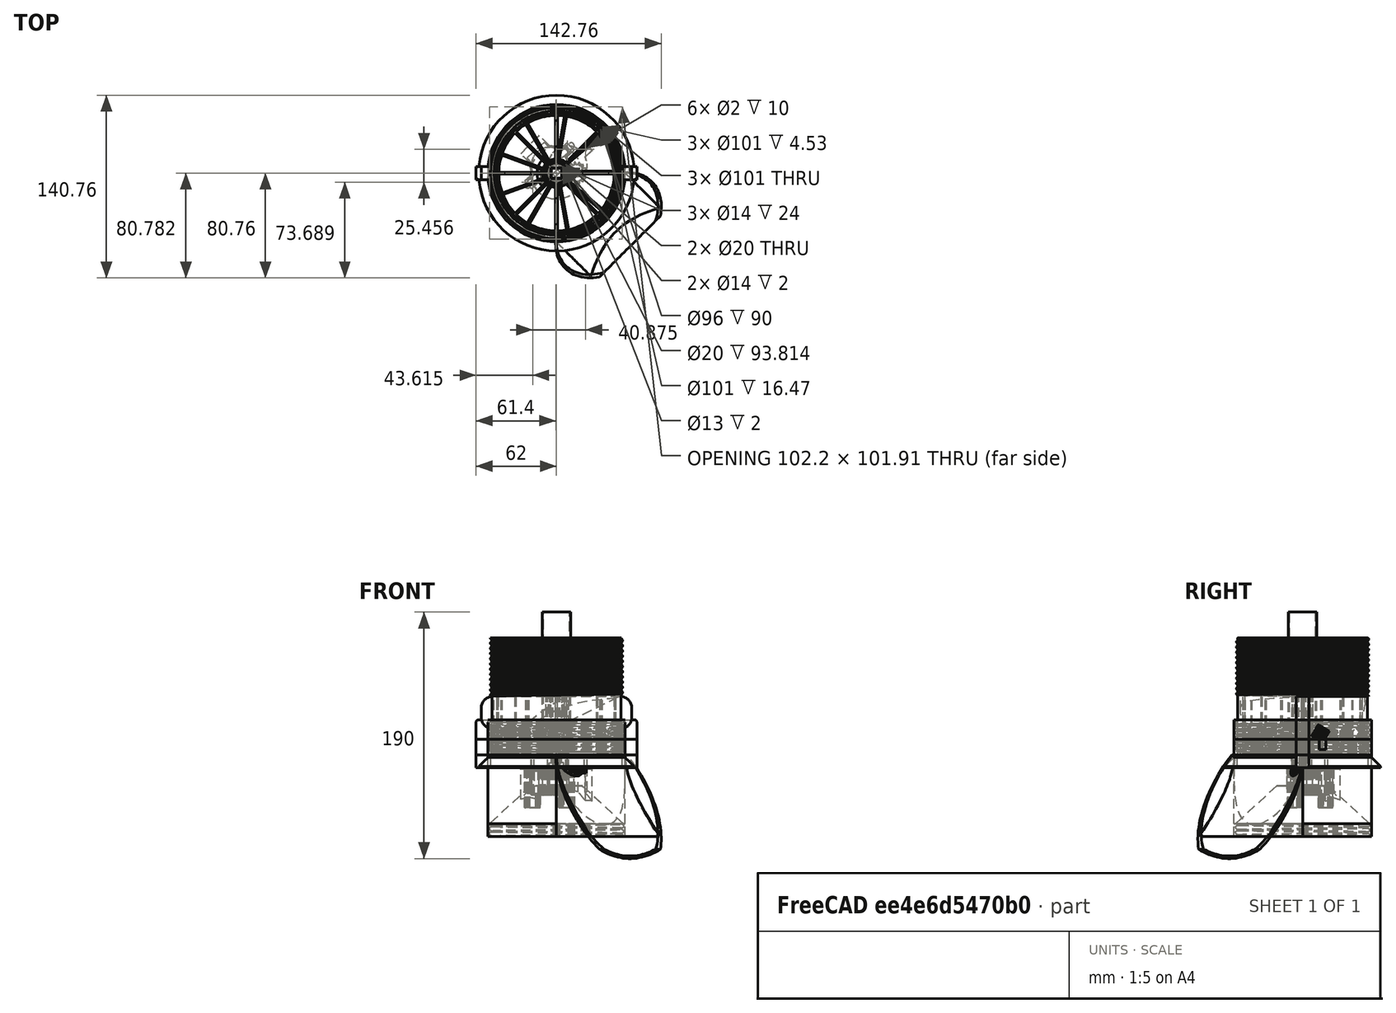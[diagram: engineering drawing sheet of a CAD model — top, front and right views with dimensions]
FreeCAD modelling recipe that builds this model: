
FCSTD DOCUMENT  (FreeCAD 0.19R24291 (Git))
Label: Small
License: CreativeCommons Attribution-NonCommercial
LicenseURL: http://creativecommons.org/licenses/by-nc/4.0/
objects: Part::Box×39, Part::Cylinder×30, Part::MultiFuse×25, Part::Cut×24, Part::FeaturePython×21, Part::Cone×11, App::DocumentObjectGroup×9, Part::Helix×5, PartDesign::FeatureBase×5, Sketcher::SketchObject×5, Part::Sweep×5, Part::Feature×5, Part::Fillet×3, PartDesign::Body×2, Part::Chamfer×1
note: 181 computed .brp shape members not serialized (recipe doc carries the construction recipe); baked Part::Feature solids carry a one-line shape summary decoded from their .brp

FEATURE [Part::Cylinder] Cylinder
  Angle = 270
  AttacherType = Attacher::AttachEngine3D
  Height = 2
  Radius = 53
FEATURE [Part::Box] Box  label="Cube"
  AttacherType = Attacher::AttachEngine3D
  Height = 60
  Length = 100
  Placement = pos=(-47,-0.8,0) rot=(0,0,1;0rad)
  Width = 1.5
FEATURE [Part::FeaturePython] Tube  # WARN: FeaturePython — macro-defined, semantics opaque (R4)
  Height = 60
  InnerRadius = 44.5
  OuterRadius = 46
FEATURE [Part::Box] Box003  label="Cube003"
  AttacherType = Attacher::AttachEngine3D
  Height = 60
  Length = 100
  Placement = pos=(-0.8,48.5,0) rot=(0,0,-1;1.5708rad)
  Width = 1.5
FEATURE [Part::Cylinder] Cylinder001
  Angle = 360
  AttacherType = Attacher::AttachEngine3D
  Height = 60
  Radius = 8
FEATURE [Part::Box] Box004  label="Cube004"
  AttacherType = Attacher::AttachEngine3D
  Height = 60
  Length = 8.3
  Placement = pos=(-4.15,-4.15,0) rot=(0,0,1;0rad)
  Width = 8.3
FEATURE [Part::Cone] Cone
  Angle = 360
  AttacherType = Attacher::AttachEngine3D
  Height = 10
  Placement = pos=(0,0,2) rot=(0,0,1;0rad)
  Radius1 = 7
  Radius2 = 4
FEATURE [Part::FeaturePython] Tube001  label="Tube001_out"  # WARN: FeaturePython — macro-defined, semantics opaque (R4)
  Height = 132
  InnerRadius = 48
  OuterRadius = 50
FEATURE [Part::FeaturePython] Tube002  # WARN: FeaturePython — macro-defined, semantics opaque (R4)
  Height = 2
  InnerRadius = 46
  OuterRadius = 53
FEATURE [Part::FeaturePython] Tube003  # WARN: FeaturePython — macro-defined, semantics opaque (R4)
  Height = 2
  InnerRadius = 4
  OuterRadius = 8.5
FEATURE [Part::Cylinder] Cylinder002
  Angle = 360
  AttacherType = Attacher::AttachEngine3D
  Height = 2
  Radius = 6.5
FEATURE [Part::Cone] Cone001
  Angle = 360
  AttacherType = Attacher::AttachEngine3D
  Height = 30
  Radius1 = 9
  Radius2 = 4
FEATURE [Part::Helix] Helix  label="Helix_in"
  Angle = 0
  AttacherType = Attacher::AttachEngine3D
  Height = 63
  LocalCoord = 0
  Pitch = 4
  Radius = 50
  Style = 1
FEATURE [PartDesign::FeatureBase] BaseFeature
  BaseFeature = -> Helix
FEATURE [Sketcher::SketchObject] Sketch
  ExternalGeometry = -> [BaseFeature]
  FullyConstrained = false
  MapMode = 5
  Placement = pos=(0,0,0) rot=(0.57735,0.57735,0.57735;2.0944rad)
  Support = -> [YZ_Plane]
  sketch-geometry (1):
    g0: Circle CenterX=-50 CenterY=63 CenterZ=0 NormalX=0 NormalY=0 NormalZ=1 AngleXU=0 Radius=1
  constraints (2):
    c: Radius(g0) = 1
    c: Coincident(g0,g-3)
FEATURE [PartDesign::Body] Body
  BaseFeature = -> Helix
  Group = -> [BaseFeature,Sketch]
  Origin = -> Origin
  Tip = -> BaseFeature
FEATURE [Part::Sweep] Sweep  label="Sweep_in"
  Frenet = true
  Sections = -> [Sketch]
  Solid = true
  Spine = -> BaseFeature [Edge16,Edge15,Edge14,Edge13,Edge12,Edge11,Edge10,Edge9,Edge8,Edge7,Edge6,Edge5,Edge4,Edge3,Edge2,Edge1]
  Transition = 1
FEATURE [Part::FeaturePython] Tube004  # WARN: FeaturePython — macro-defined, semantics opaque (R4)
  Height = 20
  InnerRadius = 50
  OuterRadius = 53
  Placement = pos=(0,0,25) rot=(0,0,1;0rad)
FEATURE [Part::Cylinder] Cylinder004
  Angle = 360
  AttacherType = Attacher::AttachEngine3D
  Height = 63
  Placement = pos=(0,0,90) rot=(0,0,1;0rad)
  Radius = 55
FEATURE [Part::Cylinder] Cylinder005
  Angle = 360
  AttacherType = Attacher::AttachEngine3D
  Height = 5
  Placement = pos=(0,0,-5) rot=(0,0,1;0rad)
  Radius = 55
FEATURE [Part::MultiFuse] Fusion003
  Shapes = -> [Tube004,Cylinder004,Cylinder005]
FEATURE [Part::Helix] Helix001  label="Helix_out"
  Angle = 0
  AttacherType = Attacher::AttachEngine3D
  Height = 63
  LocalCoord = 0
  Pitch = 4
  Radius = 50.2
  Style = 1
FEATURE [Part::FeaturePython] Tube005  label="Tube_out_cover"  # WARN: FeaturePython — macro-defined, semantics opaque (R4)
  Height = 10
  InnerRadius = 50.5
  OuterRadius = 53
FEATURE [PartDesign::FeatureBase] BaseFeature001
  BaseFeature = -> Helix001
FEATURE [Sketcher::SketchObject] Sketch001
  ExternalGeometry = -> [BaseFeature001]
  FullyConstrained = false
  MapMode = 5
  Placement = pos=(0,0,0) rot=(1,0,0;1.5708rad)
  Support = -> [XZ_Plane001]
  sketch-geometry (1):
    g0: Circle CenterX=50.2 CenterY=0 CenterZ=0 NormalX=0 NormalY=0 NormalZ=1 AngleXU=0 Radius=1.5
  constraints (2):
    c: Radius(g0) = 1.5
    c: Coincident(g0,g-3)
FEATURE [PartDesign::Body] Body001
  BaseFeature = -> Helix001
  Group = -> [BaseFeature001,Sketch001]
  Origin = -> Origin001
  Tip = -> BaseFeature001
FEATURE [Part::Sweep] Sweep001  label="Sweep_out"
  Frenet = true
  Sections = -> [Sketch001]
  Solid = true
  Spine = -> BaseFeature001 [Edge1,Edge2,Edge3,Edge4,Edge5,Edge6,Edge7,Edge8,Edge9,Edge10,Edge11,Edge12,Edge13,Edge14,Edge15,Edge16]
  Transition = 1
FEATURE [App::DocumentObjectGroup] Group  label="Cut_okraj"
  Group = -> [Body001,Helix001,Sweep001]
FEATURE [Part::Cut] Cut002  label="Cut_kryt001"
  Base = -> Tube005
  Placement = pos=(0,0,2) rot=(0,0,1;0rad)
  Tool = -> Sweep001
FEATURE [Part::MultiFuse] Fusion004
  Shapes = -> [Cylinder,Tube003,Tube002,Cut002]
FEATURE [Part::Cut] Cut003  label="Cut003_vrch"
  Base = -> Fusion004
  Tool = -> Cylinder002
FEATURE [Part::Cylinder] Cylinder006
  Angle = 360
  AttacherType = Attacher::AttachEngine3D
  Height = 53
  Placement = pos=(0,0,-53) rot=(0,0,1;0rad)
  Radius = 53
FEATURE [Part::Cylinder] Cylinder007
  Angle = 360
  AttacherType = Attacher::AttachEngine3D
  Height = 45
  Placement = pos=(0,0,-43) rot=(0,0,1;0rad)
  Radius = 8.5
FEATURE [Part::FeaturePython] Tube009  # WARN: FeaturePython — macro-defined, semantics opaque (R4)
  Height = 53
  InnerRadius = 7
  OuterRadius = 8.5
  Placement = pos=(0,0,-53) rot=(0,0,1;0rad)
FEATURE [Part::Cone] Cone002  label="Cone002_vonkajsi"
  Angle = 180
  AttacherType = Attacher::AttachEngine3D
  Height = 80
  Placement = pos=(0,0,0) rot=(-0.281085,0.678598,-0.678598;2.59356rad)
  Radius1 = 2
  Radius2 = 80
FEATURE [Part::Cone] Cone003
  Angle = 180
  AttacherType = Attacher::AttachEngine3D
  Height = 80
  Placement = pos=(0,0,0) rot=(-0.281085,0.678598,-0.678598;2.59356rad)
  Radius1 = 2
  Radius2 = 78
FEATURE [Part::Box] Box005  label="Cube005"
  AttacherType = Attacher::AttachEngine3D
  Height = 50
  Length = 100
  Placement = pos=(-38.1838,-91.9239,0) rot=(0.318976,0.770076,-0.552483;1.28666rad)
  Width = 200
FEATURE [Part::FeaturePython] Tube012  label="Tube_out_cover001"  # WARN: FeaturePython — macro-defined, semantics opaque (R4)
  Height = 10
  InnerRadius = 50.5
  OuterRadius = 53
FEATURE [Part::Cylinder] Cylinder008
  Angle = 360
  AttacherType = Attacher::AttachEngine3D
  Height = 2
  Radius = 53
FEATURE [Part::Helix] Helix002  label="Helix_out001"
  Angle = 0
  AttacherType = Attacher::AttachEngine3D
  Height = 63
  LocalCoord = 0
  Pitch = 4
  Radius = 50.2
  Style = 1
FEATURE [PartDesign::FeatureBase] BaseFeature002
  BaseFeature = -> Helix002
FEATURE [Sketcher::SketchObject] Sketch002
  ExternalGeometry = -> [BaseFeature002]
  FullyConstrained = false
  MapMode = 5
  Placement = pos=(0,0,0) rot=(1,0,0;1.5708rad)
  Support = -> [XZ_Plane002]
  sketch-geometry (1):
    g0: Circle CenterX=50.2 CenterY=0 CenterZ=0 NormalX=0 NormalY=0 NormalZ=1 AngleXU=0 Radius=1.5
  constraints (2):
    c: Radius(g0) = 1.5
    c: Coincident(g0,g-3)
FEATURE [Part::Sweep] Sweep002  label="Sweep_out001"
  Frenet = true
  Sections = -> [Sketch002]
  Solid = true
  Spine = -> BaseFeature002 [Edge1,Edge2,Edge3,Edge4,Edge5,Edge6,Edge7,Edge8,Edge9,Edge10,Edge11,Edge12,Edge13,Edge14,Edge15,Edge16]
  Transition = 1
FEATURE [Part::Cut] Cut008  label="Cut_kryt002"
  Base = -> Tube012
  Placement = pos=(0,0,2) rot=(0,0,1;0rad)
  Tool = -> Sweep002
FEATURE [Part::Box] Box006  label="Cube006"
  AttacherType = Attacher::AttachEngine3D
  Height = 12
  Length = 10
  Placement = pos=(52,-5,0) rot=(0,0,1;0rad)
  Width = 10
FEATURE [Part::Box] Box007  label="Cube007"
  AttacherType = Attacher::AttachEngine3D
  Height = 12
  Length = 10
  Placement = pos=(-62,-5,0) rot=(0,0,1;0rad)
  Width = 10
FEATURE [Part::MultiFuse] Fusion007
  Shapes = -> [Cylinder008,Cut008,Box006,Box007]
FEATURE [App::DocumentObjectGroup] Group005  label="horna_krytka"
  Group = -> [BaseFeature002,XZ_Plane002,Helix002,Fusion007]
FEATURE [Part::Box] Box008  label="Cube008"
  AttacherType = Attacher::AttachEngine3D
  Height = 25
  Length = 10
  Placement = pos=(48,-5,20) rot=(0,0,1;0rad)
  Width = 10
FEATURE [Part::Box] Box009  label="Cube009"
  AttacherType = Attacher::AttachEngine3D
  Height = 25
  Length = 10
  Placement = pos=(-58,-5,20) rot=(0,0,1;0rad)
  Width = 10
FEATURE [Part::MultiFuse] Fusion008
  Shapes = -> [Box008,Box009]
FEATURE [Part::Feature] Step_28BYJ_48_V2_positive_CUT001001_solid  label="Step_28BYJ_48_V2_positive_CUT002 (Solid)"
  Placement = pos=(-5.40614,5.8826,-21) rot=(0,0,-1;0.837758rad)
  shape: bbox 38.19 x 35.33 x 39.75 mm, 702 faces (baked)
FEATURE [Part::Cylinder] Cylinder009
  Angle = 360
  AttacherType = Attacher::AttachEngine3D
  Height = 80
  Placement = pos=(-5.42314,5.90251,-91) rot=(0,0,1;0.680678rad)
  Radius = 15
FEATURE [Part::Box] Box010  label="Cube010"
  AttacherType = Attacher::AttachEngine3D
  Height = 80
  Length = 44
  Placement = pos=(-19.1279,-11.9828,-91) rot=(0,0,1;0.733038rad)
  Width = 8
FEATURE [Part::Box] Box011  label="Cube011"
  AttacherType = Attacher::AttachEngine3D
  Height = 80
  Length = 20
  Placement = pos=(-19.799,7.07107,-91) rot=(0,0,1;0.785398rad)
  Width = 11
FEATURE [Part::Box] Box012  label="Cube012"
  AttacherType = Attacher::AttachEngine3D
  Height = 10
  Length = 8
  Placement = pos=(-3.18198,-3.88909,0) rot=(0,0,1;0rad)
  Width = 8
FEATURE [Part::Cone] Cone004
  Angle = 360
  AttacherType = Attacher::AttachEngine3D
  Height = 29
  Placement = pos=(0,0,-53) rot=(0,0,1;0rad)
  Radius1 = 51.5
  Radius2 = 20
FEATURE [Part::Cylinder] Cylinder010
  Angle = 360
  AttacherType = Attacher::AttachEngine3D
  Height = 10
  Placement = pos=(-18.3848,-7.07107,-11) rot=(0,0,1;0.785398rad)
  Radius = 1
FEATURE [Part::Cylinder] Cylinder011
  Angle = 360
  AttacherType = Attacher::AttachEngine3D
  Height = 10
  Placement = pos=(8.48528,18.3848,-11) rot=(0,0,1;0.785398rad)
  Radius = 1
FEATURE [Part::MultiFuse] Fusion010
  Shapes = -> [Box011,Cylinder009,Box010,Cone004,Cylinder010,Cylinder011]
FEATURE [Part::Feature] Cut002001  label="Cut_kryt003"
  Placement = pos=(0,0,-63) rot=(0,0,1;0rad)
  shape: bbox 111.8 x 118.9 x 17.7 mm, 14 faces (baked)
FEATURE [Part::Feature] Cut009001  label="Cut009_middle001"
  shape: bbox 166.1 x 166.1 x 80 mm, 45 faces (baked)
FEATURE [Part::Cylinder] Cylinder013
  Angle = 360
  AttacherType = Attacher::AttachEngine3D
  Height = 3
  Placement = pos=(0,0,-9) rot=(0,0,1;0rad)
  Radius = 5.6
FEATURE [Part::Box] Box014  label="Cube014"
  AttacherType = Attacher::AttachEngine3D
  Height = 40
  Length = 7.9
  Placement = pos=(-4,-4,-6) rot=(0,0,1;0rad)
  Width = 7.9
FEATURE [Part::Cylinder] Cylinder014
  Angle = 360
  AttacherType = Attacher::AttachEngine3D
  Height = 2
  Radius = 7
FEATURE [Part::Box] Box016  label="Cube016"
  AttacherType = Attacher::AttachEngine3D
  Height = 100
  Length = 100
  Placement = pos=(-71.3207,-123.154,-92) rot=(0,0,-1;0.785398rad)
  Width = 100
FEATURE [Part::Box] Box017  label="Cube017"
  AttacherType = Attacher::AttachEngine3D
  Height = 100
  Length = 100
  Placement = pos=(53.0309,0.0406241,-92) rot=(0,0,-1;0.785398rad)
  Width = 100
FEATURE [Part::Box] Box018  label="Cube018"
  AttacherType = Attacher::AttachEngine3D
  Height = 200
  Length = 200
  Placement = pos=(-111,-128,-263) rot=(0,0,1;0rad)
  Width = 200
FEATURE [Part::MultiFuse] Fusion009004
  Shapes = -> [Cone003,Box016,Box017,Box018]
FEATURE [Part::Cut] Cut004  label="Cut004_len_lievik"
  Base = -> Cone002
  Tool = -> Fusion009004
FEATURE [Part::Cut] Cut007
  Base = -> Cut004
  Tool = -> Box005
FEATURE [Part::Box] Box019  label="Cube019"
  AttacherType = Attacher::AttachEngine3D
  Height = 63
  Length = 38
  Placement = pos=(-0.609979,-52.4438,-63) rot=(0,0,-1;0.785398rad)
  Width = 75
FEATURE [Part::Cylinder] Cylinder018
  Angle = 360
  AttacherType = Attacher::AttachEngine3D
  Height = 60
  Placement = pos=(0,0,-63) rot=(0,0,1;0rad)
  Radius = 53
FEATURE [Part::Cut] Cut009005
  Base = -> Box019
  Tool = -> Cylinder018
FEATURE [Part::MultiFuse] Fusion009005
  Shapes = -> [Cylinder006,Cut009005]
FEATURE [Part::Cut] Cut005  label="Cut005_okraj_stena"
  Base = -> Fusion009005
  Tool = -> Cone002
FEATURE [Part::MultiFuse] Fusion005
  Shapes = -> [Cut005,Cut007]
FEATURE [Part::Cut] Cut006
  Base = -> Fusion005
  Tool = -> Cylinder007
FEATURE [Part::MultiFuse] Fusion006  label="spodok"
  Shapes = -> [Tube009,Cut006]
FEATURE [Part::Cut] Cut009  label="Cut009_middle"
  Base = -> Fusion006
  Tool = -> Fusion010
FEATURE [App::DocumentObjectGroup] Group004  label="Spodok"
  Group = -> [Cut003,Cut009,Cut002001]
FEATURE [Part::Fillet] Fillet
  Base = -> Fusion008
  Edges = 4 edges r=9: [Edge6,Edge8,Edge14,Edge16]
FEATURE [Part::Box] Box020  label="Cube020"
  AttacherType = Attacher::AttachEngine3D
  Height = 37
  Length = 10
  Placement = pos=(52,-5,-10) rot=(0,0,1;0rad)
  Width = 10
FEATURE [Part::Cylinder] Cylinder019
  Angle = 360
  AttacherType = Attacher::AttachEngine3D
  Height = 1
  Placement = pos=(0,0,-10) rot=(0,0,1;0rad)
  Radius = 53
FEATURE [Part::Box] Box021  label="Cube021"
  AttacherType = Attacher::AttachEngine3D
  Height = 37
  Length = 10
  Placement = pos=(-62,-5,-10) rot=(0,0,1;0rad)
  Width = 10
FEATURE [Part::FeaturePython] Tube013  label="Tube_out_cover002"  # WARN: FeaturePython — macro-defined, semantics opaque (R4)
  Height = 25
  InnerRadius = 50.5
  OuterRadius = 53
FEATURE [Part::Helix] Helix003  label="Helix_out002"
  Angle = 0
  AttacherType = Attacher::AttachEngine3D
  Height = 63
  LocalCoord = 0
  Pitch = 4
  Radius = 50.2
  Style = 1
FEATURE [PartDesign::FeatureBase] BaseFeature003
  BaseFeature = -> Helix003
FEATURE [Sketcher::SketchObject] Sketch003
  ExternalGeometry = -> [BaseFeature003]
  FullyConstrained = false
  MapMode = 5
  Placement = pos=(0,0,0) rot=(1,0,0;1.5708rad)
  Support = -> [XZ_Plane003]
  sketch-geometry (1):
    g0: Circle CenterX=50.2 CenterY=0 CenterZ=0 NormalX=0 NormalY=0 NormalZ=1 AngleXU=0 Radius=1.5
  constraints (2):
    c: Radius(g0) = 1.5
    c: Coincident(g0,g-3)
FEATURE [Part::Sweep] Sweep003  label="Sweep_out002"
  Frenet = true
  Sections = -> [Sketch003]
  Solid = true
  Spine = -> BaseFeature003 [Edge1,Edge2,Edge3,Edge4,Edge5,Edge6,Edge7,Edge8,Edge9,Edge10,Edge11,Edge12,Edge13,Edge14,Edge15,Edge16]
  Transition = 1
FEATURE [Part::Cut] Cut009006  label="Cut_kryt004"
  Base = -> Tube013
  Placement = pos=(0,0,2) rot=(0,0,1;0rad)
  Tool = -> Sweep003
FEATURE [Part::FeaturePython] Tube014  label="Tube_out_cover003"  # WARN: FeaturePython — macro-defined, semantics opaque (R4)
  Height = 20
  InnerRadius = 50.5
  OuterRadius = 53
  Placement = pos=(0,0,-10) rot=(0,0,1;0rad)
FEATURE [Part::Box] Box022  label="Cube022"
  AttacherType = Attacher::AttachEngine3D
  Height = 10
  Length = 10
  Placement = pos=(84.8787,7,14.5355) rot=(-0.250563,0.250563,0.935113;1.63783rad)
  Width = 156
FEATURE [Part::Box] Box023  label="Cube023"
  AttacherType = Attacher::AttachEngine3D
  Height = 10
  Length = 5
  Placement = pos=(61.306,12.7496,4) rot=(0,0,1;1.5708rad)
  Width = 150
FEATURE [Part::MultiFuse] Fusion009007
  Shapes = -> [Box022,Box023]
FEATURE [Part::Box] Box024  label="Cube024"
  AttacherType = Attacher::AttachEngine3D
  Height = 60
  Length = 100
  Placement = pos=(-32.9993,-34.0926,0) rot=(0,0,1;0.785398rad)
  Width = 1.5
FEATURE [Part::Box] Box025  label="Cube025"
  AttacherType = Attacher::AttachEngine3D
  Height = 60
  Length = 100
  Placement = pos=(34.388,-33.4562,0) rot=(0,0,1;2.35619rad)
  Width = 1.5
FEATURE [Part::MultiFuse] Fusion
  Shapes = -> [Box,Box003,Cylinder001,Tube,Cone001,Box024,Box025]
FEATURE [Part::FeaturePython] Tube015  # WARN: FeaturePython — macro-defined, semantics opaque (R4)
  Height = 60
  InnerRadius = 46
  OuterRadius = 60
FEATURE [Part::MultiFuse] Fusion001
  Shapes = -> [Box004,Cone,Cylinder014,Tube015]
FEATURE [Part::Cut] Cut  label="Cut_vnutro"
  Base = -> Fusion
  Placement = pos=(0,0,2.5) rot=(0,0,1;0rad)
  Tool = -> Fusion001
FEATURE [App::DocumentObjectGroup] Group003  label="Rotacia_6"
  Group = -> [Cut]
FEATURE [Part::Box] Box026  label="Cube026"
  AttacherType = Attacher::AttachEngine3D
  Height = 60
  Length = 50
  Width = 1.5
FEATURE [Part::Cone] Cone005
  Angle = 360
  AttacherType = Attacher::AttachEngine3D
  Height = 10
  Placement = pos=(0,0,2) rot=(0,0,1;0rad)
  Radius1 = 7
  Radius2 = 4
FEATURE [Part::Cone] Cone006
  Angle = 360
  AttacherType = Attacher::AttachEngine3D
  Height = 30
  Radius1 = 9
  Radius2 = 4
FEATURE [Part::FeaturePython] Tube016  # WARN: FeaturePython — macro-defined, semantics opaque (R4)
  Height = 60
  InnerRadius = 45
  OuterRadius = 46
FEATURE [Part::Cylinder] Cylinder020
  Angle = 360
  AttacherType = Attacher::AttachEngine3D
  Height = 60
  Radius = 8
FEATURE [Part::Box] Box028  label="Cube028"
  AttacherType = Attacher::AttachEngine3D
  Height = 60
  Length = 8.4
  Placement = pos=(-4.2,-4.2,0) rot=(0,0,1;0rad)
  Width = 8.4
FEATURE [Part::Cylinder] Cylinder021
  Angle = 360
  AttacherType = Attacher::AttachEngine3D
  Height = 2
  Radius = 7
FEATURE [Part::FeaturePython] Tube017  # WARN: FeaturePython — macro-defined, semantics opaque (R4)
  Height = 60
  InnerRadius = 46
  OuterRadius = 60
FEATURE [Part::MultiFuse] Fusion009008
  Shapes = -> [Box028,Cone005,Cylinder021,Tube017]
FEATURE [Part::Box] Box029  label="Cube029"
  AttacherType = Attacher::AttachEngine3D
  Height = 60
  Length = 50
  Placement = pos=(0,0,0) rot=(0,0,1;0.698132rad)
  Width = 1.5
FEATURE [Part::Box] Box030  label="Cube030"
  AttacherType = Attacher::AttachEngine3D
  Height = 60
  Length = 50
  Placement = pos=(0,0,0) rot=(0,0,1;1.39626rad)
  Width = 1.5
FEATURE [Part::Box] Box031  label="Cube031"
  AttacherType = Attacher::AttachEngine3D
  Height = 60
  Length = 50
  Placement = pos=(0,0,0) rot=(0,0,1;2.0944rad)
  Width = 1.5
FEATURE [Part::Box] Box032  label="Cube032"
  AttacherType = Attacher::AttachEngine3D
  Height = 60
  Length = 50
  Placement = pos=(0,0,0) rot=(0,0,1;2.79253rad)
  Width = 1.5
FEATURE [Part::Box] Box033  label="Cube033"
  AttacherType = Attacher::AttachEngine3D
  Height = 60
  Length = 50
  Placement = pos=(0,0,0) rot=(0,0,1;3.49066rad)
  Width = 1.5
FEATURE [Part::Box] Box034  label="Cube034"
  AttacherType = Attacher::AttachEngine3D
  Height = 60
  Length = 50
  Placement = pos=(0,0,0) rot=(0,0,-1;0.698132rad)
  Width = 1.5
FEATURE [Part::Box] Box035  label="Cube035"
  AttacherType = Attacher::AttachEngine3D
  Height = 60
  Length = 50
  Placement = pos=(0,0,0) rot=(0,0,1;4.88692rad)
  Width = 1.5
FEATURE [Part::Box] Box036  label="Cube036"
  AttacherType = Attacher::AttachEngine3D
  Height = 60
  Length = 50
  Placement = pos=(0,0,0) rot=(0,0,1;4.18879rad)
  Width = 1.5
FEATURE [Part::Box] Box037  label="Cube037"
  AttacherType = Attacher::AttachEngine3D
  Height = 60
  Length = 50
  Placement = pos=(0,0,0) rot=(0,0,1;3.49066rad)
  Width = 1.5
FEATURE [Part::MultiFuse] Fusion009009
  Shapes = -> [Box026,Cylinder020,Tube016,Cone006,Box029,Box030,Box031,Box032,Box033,Box034,Box035,Box036,Box037]
FEATURE [Part::Cut] Cut009008  label="Cut_vnutro001"
  Base = -> Fusion009009
  Tool = -> Fusion009008
FEATURE [App::DocumentObjectGroup] Group009  label="Rotacia_9"
  Group = -> [Cut009008]
FEATURE [Part::FeaturePython] involutegear  # WARN: FeaturePython — macro-defined, semantics opaque (R4)
  AttacherType = Attacher::AttachEngine3D
  Placement = pos=(0,0,-14) rot=(0,0,1;0rad)
  backlash = 0
  beta = 0
  clearance = 0.25
  da = 17
  df = 12.5
  double_helix = false
  dw = 15
  head = 0
  height = 5
  module = 1
  numpoints = 6
  pressure_angle = 20
  properties_from_tool = false
  reversed_backlash = false
  shift = 0
  simple = false
  teeth = 15
  transverse_pitch = 3.14159
  undercut = false
  version = 0.0.3
FEATURE [Part::MultiFuse] Fusion011
  Shapes = -> [Box014,Cylinder013,involutegear]
FEATURE [App::DocumentObjectGroup] Group006  label="Hriadel"
  Group = -> [Fusion011]
FEATURE [Part::Box] Box038  label="Cube038"
  AttacherType = Attacher::AttachEngine3D
  Height = 50
  Length = 100
  Placement = pos=(-38.1838,-91.9239,0) rot=(0.318976,0.770076,-0.552483;1.28666rad)
  Width = 200
FEATURE [Part::Box] Box039  label="Cube039"
  AttacherType = Attacher::AttachEngine3D
  Height = 80
  Length = 44
  Placement = pos=(-5.13,-11.9828,-91) rot=(0,0,1;0.733038rad)
  Width = 8
FEATURE [Part::Cylinder] Cylinder022
  Angle = 360
  AttacherType = Attacher::AttachEngine3D
  Height = 80
  Placement = pos=(8.58,5.90251,-91) rot=(0,0,1;0.680678rad)
  Radius = 15
FEATURE [Part::Cylinder] Cylinder023
  Angle = 360
  AttacherType = Attacher::AttachEngine3D
  Height = 10
  Placement = pos=(-18.38,-7.07107,-11) rot=(0,0,1;0.785398rad)
  Radius = 1
FEATURE [Part::Cylinder] Cylinder024
  Angle = 360
  AttacherType = Attacher::AttachEngine3D
  Height = 10
  Placement = pos=(22.49,18.3848,-11) rot=(0,0,1;0.785398rad)
  Radius = 1
FEATURE [Part::Cylinder] Cylinder025
  Angle = 360
  AttacherType = Attacher::AttachEngine3D
  Height = 53
  Placement = pos=(0,0,-53) rot=(0,0,1;0rad)
  Radius = 53
FEATURE [Part::Cylinder] Cylinder026
  Angle = 360
  AttacherType = Attacher::AttachEngine3D
  Height = 45
  Placement = pos=(0,0,-43) rot=(0,0,1;0rad)
  Radius = 8.5
FEATURE [Part::FeaturePython] Tube018  # WARN: FeaturePython — macro-defined, semantics opaque (R4)
  Height = 53
  InnerRadius = 7
  OuterRadius = 8.5
  Placement = pos=(0,0,-53) rot=(0,0,1;0rad)
FEATURE [Part::Box] Box041  label="Cube041"
  AttacherType = Attacher::AttachEngine3D
  Height = 100
  Length = 100
  Placement = pos=(-71.3207,-123.154,-92) rot=(0,0,-1;0.785398rad)
  Width = 100
FEATURE [Part::Box] Box042  label="Cube042"
  AttacherType = Attacher::AttachEngine3D
  Height = 100
  Length = 100
  Placement = pos=(53.0309,0.0406241,-92) rot=(0,0,-1;0.785398rad)
  Width = 100
FEATURE [Part::Box] Box043  label="Cube043"
  AttacherType = Attacher::AttachEngine3D
  Height = 200
  Length = 200
  Placement = pos=(-111,-128,-263) rot=(0,0,1;0rad)
  Width = 200
FEATURE [Part::Box] Box044  label="Cube044"
  AttacherType = Attacher::AttachEngine3D
  Height = 63
  Length = 38
  Placement = pos=(-0.609979,-52.4438,-63) rot=(0,0,-1;0.785398rad)
  Width = 75
FEATURE [Part::Cylinder] Cylinder027
  Angle = 360
  AttacherType = Attacher::AttachEngine3D
  Height = 60
  Placement = pos=(0,0,-63) rot=(0,0,1;0rad)
  Radius = 53
FEATURE [Part::Helix] Helix004  label="Helix_out003"
  Angle = 0
  AttacherType = Attacher::AttachEngine3D
  Height = 63
  LocalCoord = 0
  Pitch = 4
  Radius = 50.2
  Style = 1
FEATURE [PartDesign::FeatureBase] BaseFeature004
  BaseFeature = -> Helix004
FEATURE [Part::FeaturePython] Tube019  # WARN: FeaturePython — macro-defined, semantics opaque (R4)
  Height = 2
  InnerRadius = 46
  OuterRadius = 53
FEATURE [Part::FeaturePython] Tube020  # WARN: FeaturePython — macro-defined, semantics opaque (R4)
  Height = 2
  InnerRadius = 4
  OuterRadius = 8.5
FEATURE [Sketcher::SketchObject] Sketch004
  ExternalGeometry = -> [BaseFeature004]
  FullyConstrained = false
  MapMode = 5
  Placement = pos=(0,0,0) rot=(1,0,0;1.5708rad)
  Support = -> [XZ_Plane004]
  sketch-geometry (1):
    g0: Circle CenterX=50.2 CenterY=0 CenterZ=0 NormalX=0 NormalY=0 NormalZ=1 AngleXU=0 Radius=1.5
  constraints (2):
    c: Radius(g0) = 1.5
    c: Coincident(g0,g-3)
FEATURE [Part::Sweep] Sweep004  label="Sweep_out003"
  Frenet = true
  Sections = -> [Sketch004]
  Solid = true
  Spine = -> BaseFeature004 [Edge1,Edge2,Edge3,Edge4,Edge5,Edge6,Edge7,Edge8,Edge9,Edge10,Edge11,Edge12,Edge13,Edge14,Edge15,Edge16]
  Transition = 1
FEATURE [Part::FeaturePython] Tube021  label="Tube_out_cover004"  # WARN: FeaturePython — macro-defined, semantics opaque (R4)
  Height = 10
  InnerRadius = 50.5
  OuterRadius = 53
FEATURE [Part::Cone] Cone007  label="Cone002_vonkajsi001"
  Angle = 180
  AttacherType = Attacher::AttachEngine3D
  Height = 80
  Placement = pos=(0,0,0) rot=(-0.281085,0.678598,-0.678598;2.59356rad)
  Radius1 = 2
  Radius2 = 80
FEATURE [Part::Cone] Cone008
  Angle = 180
  AttacherType = Attacher::AttachEngine3D
  Height = 80
  Placement = pos=(0,0,0) rot=(-0.281085,0.678598,-0.678598;2.59356rad)
  Radius1 = 2
  Radius2 = 78
FEATURE [Part::Cone] Cone009
  Angle = 360
  AttacherType = Attacher::AttachEngine3D
  Height = 29
  Placement = pos=(0,0,-53) rot=(0,0,1;0rad)
  Radius1 = 51.5
  Radius2 = 20
FEATURE [Part::MultiFuse] Fusion009012
  Shapes = -> [Cylinder022,Box039,Cone009,Cylinder023,Cylinder024]
FEATURE [Part::Cylinder] Cylinder028
  Angle = 270
  AttacherType = Attacher::AttachEngine3D
  Height = 2
  Radius = 53
FEATURE [Part::Cylinder] Cylinder029
  Angle = 360
  AttacherType = Attacher::AttachEngine3D
  Height = 2
  Radius = 6.5
FEATURE [Part::Cut] Cut009012
  Base = -> Box044
  Tool = -> Cylinder027
FEATURE [Part::MultiFuse] Fusion009013
  Shapes = -> [Cylinder025,Cut009012]
FEATURE [Part::Cut] Cut009011  label="Cut005_okraj_stena001"
  Base = -> Fusion009013
  Tool = -> Cone007
FEATURE [Part::MultiFuse] Fusion009014
  Shapes = -> [Cone008,Box041,Box042,Box043]
FEATURE [Part::Feature] Cut009014  label="Cut_kryt005"
  Placement = pos=(0,0,-63) rot=(0,0,1;0rad)
  shape: bbox 111.8 x 118.9 x 17.7 mm, 14 faces (baked)
FEATURE [Part::Cut] Cut009015  label="Cut_kryt006"
  Base = -> Tube021
  Placement = pos=(0,0,2) rot=(0,0,1;0rad)
  Tool = -> Sweep004
FEATURE [Part::Cut] Cut009017  label="Cut004_len_lievik001"
  Base = -> Cone007
  Tool = -> Fusion009014
FEATURE [Part::Cut] Cut009009
  Base = -> Cut009017
  Tool = -> Box038
FEATURE [Part::MultiFuse] Fusion009011
  Shapes = -> [Cut009011,Cut009009]
FEATURE [Part::Cut] Cut009010
  Base = -> Fusion009011
  Tool = -> Cylinder026
FEATURE [Part::MultiFuse] Fusion009010  label="spodok001"
  Shapes = -> [Tube018,Cut009010]
FEATURE [Part::Cut] Cut009013  label="Cut009_middle002"
  Base = -> Fusion009010
  Tool = -> Fusion009012
FEATURE [Part::MultiFuse] Fusion009015
  Shapes = -> [Cylinder028,Tube020,Tube019,Cut009015]
FEATURE [Part::Cut] Cut009016  label="Cut003_vrch001"
  Base = -> Fusion009015
  Tool = -> Cylinder029
FEATURE [App::DocumentObjectGroup] Group010  label="Spodok00111"
  Group = -> [Cut009016,Cut009013,Cut009014]
FEATURE [Part::FeaturePython] involutegear001  # WARN: FeaturePython — macro-defined, semantics opaque (R4)
  AttacherType = Attacher::AttachEngine3D
  Placement = pos=(15,0,-14) rot=(0,0,1;0rad)
  backlash = 0
  beta = 0
  clearance = 0.25
  da = 17
  df = 12.5
  double_helix = false
  dw = 15
  head = 0
  height = 5
  module = 1
  numpoints = 6
  pressure_angle = 20
  properties_from_tool = false
  reversed_backlash = false
  shift = 0
  simple = false
  teeth = 15
  transverse_pitch = 3.14159
  undercut = false
  version = 0.0.3
FEATURE [Part::Fillet] Fillet001
  Base = -> Box020
  Edges = 5 edges r=2: [Edge5,Edge6,Edge7,Edge10,Edge12]
FEATURE [Part::Fillet] Fillet002
  Base = -> Box021
  Edges = 5 edges r=2: [Edge1,Edge2,Edge3,Edge10,Edge12]
FEATURE [Part::FeaturePython] Tube022  # WARN: FeaturePython — macro-defined, semantics opaque (R4)
  AttacherType = Attacher::AttachEngine3D
  Height = 8
  InnerRadius = 52
  OuterRadius = 60
  Placement = pos=(0,0,-10) rot=(0,0,1;0rad)
FEATURE [Part::Chamfer] Chamfer
  Base = -> Tube022
  Edges = 1 edges r=7: [Edge1]
FEATURE [Part::MultiFuse] Fusion009006
  Shapes = -> [Cylinder019,Cut009006,Tube014,Fillet001,Fillet002,Chamfer]
FEATURE [Part::Cut] Cut009007
  Base = -> Fusion009006
  Tool = -> Fusion009007
FEATURE [App::DocumentObjectGroup] Group008  label="dolna_krytka"
  Group = -> [BaseFeature003,XZ_Plane003,Helix003,Cut009007]
FEATURE [Part::Cylinder] Cylinder030
  Angle = 91
  AttacherType = Attacher::AttachEngine3D
  Height = 90
  Placement = pos=(0,0,11) rot=(0,0,1;2.35619rad)
  Radius = 49
FEATURE [Part::Cylinder] Cylinder031
  Angle = 360
  AttacherType = Attacher::AttachEngine3D
  Height = 40
  Placement = pos=(0,0,11) rot=(0,0,1;0rad)
  Radius = 49
FEATURE [Part::Cylinder] Cylinder032
  Angle = 360
  AttacherType = Attacher::AttachEngine3D
  Height = 115
  Placement = pos=(-86.9329,-0.374219,75.1506) rot=(0.528588,-0.00891,0.848832;3.04675rad)
  Radius = 87
FEATURE [Part::Feature] Sweep001002  label="Sweep_in001"
  Placement = pos=(0,0,56) rot=(0,0,1;0rad)
  shape: bbox 120.8 x 128.8 x 66.8 mm, 18 faces (baked)
FEATURE [Part::MultiFuse] Fusion002
  Shapes = -> [Tube001,Sweep,Sweep001002]
FEATURE [Part::Cut] Cut001  label="Cut_obal"
  Base = -> Fusion002
  Tool = -> Fusion003
FEATURE [Part::Cone] Cone010
  Angle = 360
  AttacherType = Attacher::AttachEngine3D
  Height = 5
  Placement = pos=(0,0,10) rot=(0,0,1;0rad)
  Radius1 = 8
  Radius2 = 4
FEATURE [Part::Cylinder] Cylinder033
  Angle = 91
  AttacherType = Attacher::AttachEngine3D
  Height = 90
  Placement = pos=(0,0,11) rot=(0,0,1;2.35619rad)
  Radius = 15
FEATURE [Part::Cut] Cut009019
  Base = -> Cylinder030
  Tool = -> Cylinder033
FEATURE [Part::Cylinder] Cylinder034  label="Cylinder034_delete_me"
  Angle = 360
  AttacherType = Attacher::AttachEngine3D
  Height = 40
  Placement = pos=(0,0,11) rot=(0,0,1;0rad)
  Radius = 10
FEATURE [Part::MultiFuse] Fusion009016
  Shapes = -> [Cylinder032,Cut009019,Cone010,Cylinder034]
FEATURE [Part::Cut] Cut009018
  Base = -> Cylinder031
  Tool = -> Fusion009016
FEATURE [Part::FeaturePython] Tube023  label="Tube023_delete_me"  # WARN: FeaturePython — macro-defined, semantics opaque (R4)
  AttacherType = Attacher::AttachEngine3D
  Height = 96
  InnerRadius = 10
  OuterRadius = 11
  Placement = pos=(0,0,14) rot=(0,0,1;0rad)
FEATURE [Part::MultiFuse] Fusion009
  Shapes = -> [Cut001,Fillet,Cut009018,Tube023]
FEATURE [App::DocumentObjectGroup] Group002  label="Vonkajsi_obal"
  Group = -> [Helix,Body,Fusion009]
